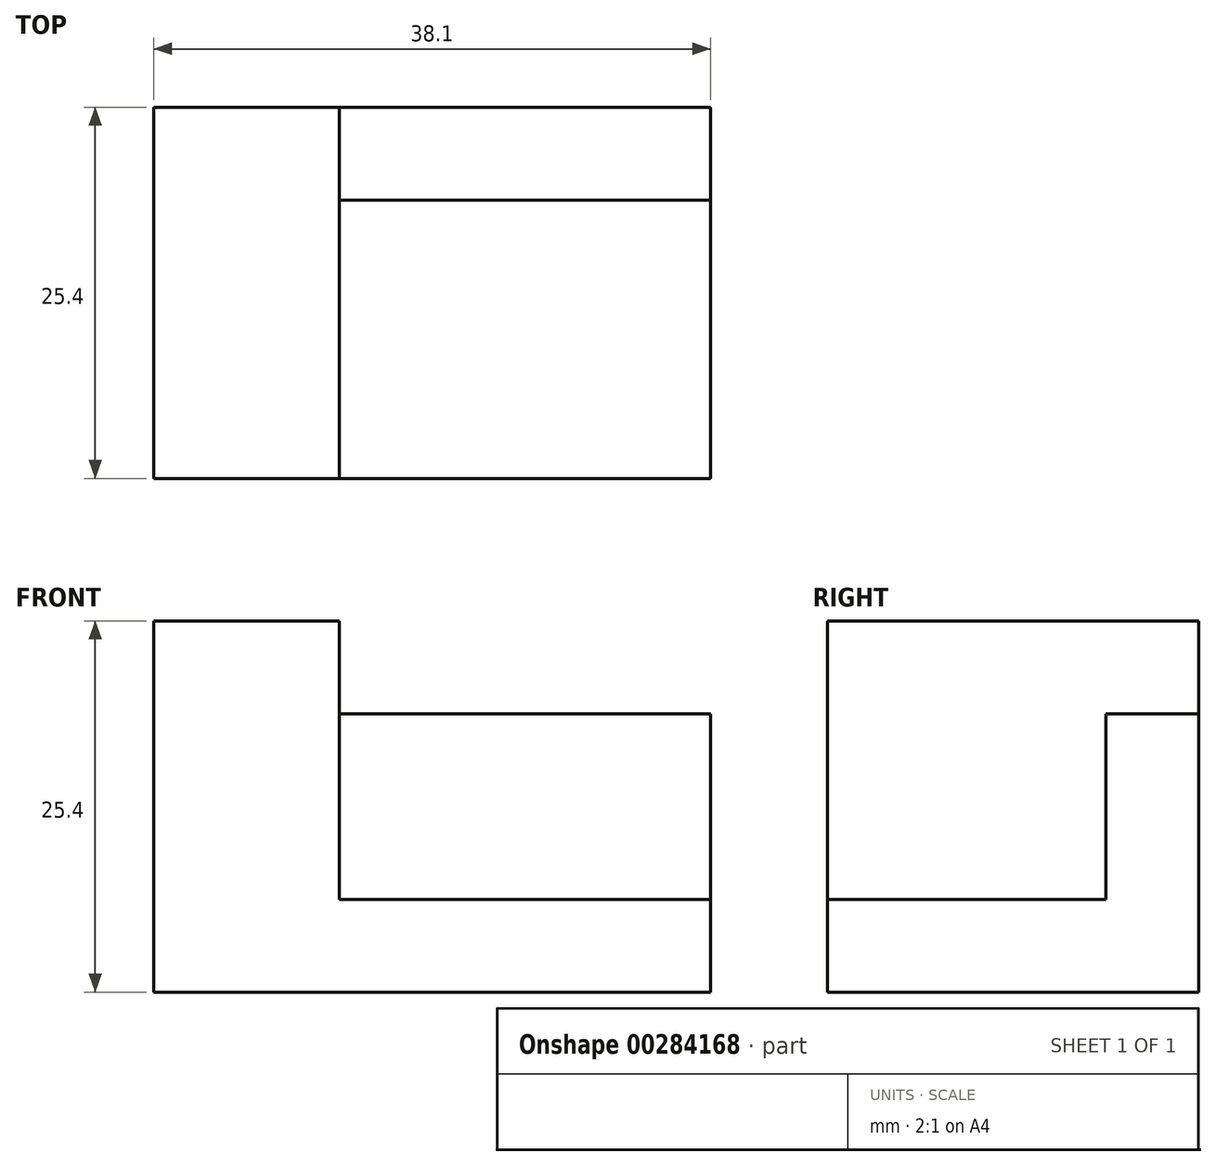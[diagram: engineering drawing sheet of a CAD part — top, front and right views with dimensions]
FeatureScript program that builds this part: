
annotation { "Feature Type Name" : "Feature", "Feature Type Description" : "" }
export const myFeature = defineFeature(function(context is Context, id is Id, definition is map)
    precondition{}
    {
        {
            var Q0;
            Q0=qCreatedBy(makeId("Front.planeOp"),FACE);
            var sketch = newSketch(context, id + "F0", { "sketchPlane" : qUnion([Q0])});
            skLineSegment(sketch, "E0.top", {"start": v(0, 25.4) * mm, "end": v(12.7, 25.4) * mm});
            skLineSegment(sketch, "E0.left", {"start": v(0, 0) * mm, "end": v(0, 25.4) * mm});
            skLineSegment(sketch, "E1", {"start": v(12.7, 25.4) * mm, "end": v(12.7, 6.35) * mm});
            skLineSegment(sketch, "E2", {"start": v(12.7, 6.35) * mm, "end": v(38.1, 6.35) * mm});
            skLineSegment(sketch, "E3", {"start": v(38.1, 6.35) * mm, "end": v(38.1, 0) * mm});
            skLineSegment(sketch, "E4", {"start": v(0, 0) * mm, "end": v(38.1, 0) * mm});
            skSolve(sketch);
        }
        {
            var Q0;
            Q0=makeQuery(id+"F0.imprint","IMPRINT",FACE,{"disambiguationData":[TD([[makeQuery(id+"F0.imprint","IMPRINT",EDGE,{"derivedFrom":sQuery(id+"F0.wireOp",EDGE,"E0.top")}),-1.0]])]});
            extrude(context, id + "F1", {"entities" : qUnion([Q0]), "depth" : 25.4 * mm});
        }
        {
            var Q0;
            Q0=qCreatedBy(makeId("Right.planeOp"),FACE);
            var sketch = newSketch(context, id + "F2", { "sketchPlane" : qUnion([Q0])});
            skLineSegment(sketch, "E5.bottom", {"start": v(0, 6.35) * mm, "end": v(-6.35, 6.35) * mm});
            skLineSegment(sketch, "E5.top", {"start": v(0, 19.05) * mm, "end": v(-6.35, 19.05) * mm});
            skLineSegment(sketch, "E5.left", {"start": v(0, 6.35) * mm, "end": v(0, 19.05) * mm});
            skLineSegment(sketch, "E5.right", {"start": v(-6.35, 6.35) * mm, "end": v(-6.35, 19.05) * mm});
            skSolve(sketch);
        }
        {
            var Q0;
            Q0 = qSketchRegion(id + "F2", true);
            extrude(context, id + "F3", {"entities" : qUnion([Q0]), "operationType" : NewBodyOperationType.ADD, "depth" : 38.1 * mm});
        }
    });
